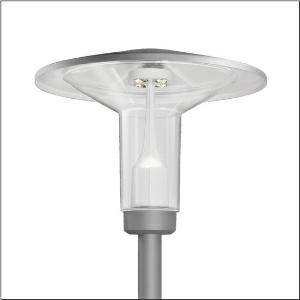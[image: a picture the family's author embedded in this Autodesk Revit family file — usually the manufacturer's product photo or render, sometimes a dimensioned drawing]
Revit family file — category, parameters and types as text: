
# Revit family: laterne_iq___st1_2a_5xa5255mf14h_e85f
name_source: partatom
category: Lighting Fixtures
units: mm (PartAtom-declared; Revit-internal decimal feet)

## family parameters
Cut with Voids When Loaded = No
Host = Face
Light Source = No
Part Type = Normal
Room Calculation Point = No
Round Connector Dimension = Use Diameter
Shared = No

## types (1)
- --- (1 x LED, 1540 lm, 11.8 W, 2700K)
    Apparent Load = 12 VA
    CIE Flux Codes = 25 63 94 98 100
    Color Rendering = 70
    Color Temperature = 2700K
    Default Elevation = 1800 mm
    Description = Lantern iQ, mast luminaire, Module 540 iQ-SR, primary light control with 3 zone facetted reflector, of plastic, silver coated, highly specular, structured, primary optical cover: cover, of PMMA, transparent, light distribution: ST1.2a, light emission: direct distribution, primary light characteristic: asymmetric, installation type: post-top, LED, High Power LED, rated luminous flux: 1.540lm, luminous efficacy: 131lm/W, light colour: 727, colour temperature: 2700K, control gear: ECG iQ, control: presetting dimming logarithmic, Street-Remote, Auto-Match, Temp-Guard, Lumen-Switch, Night-Set, Smart-Wire, Light-Fading, Desk-Remote (wireless, voltage-free reading and setting of iQ features in the workshop via application-optimized NFC function/RFID function), optimised constant luminous flux control (CLO 2.0), with terminal, 6-pole, max. 2.5mm², mains connection: 230..240V, AC, 50/60Hz, start of lifetime: 12W, end of service life: 12W, reduction: 6W, luminaire housing, upper part, of glass-fibre reinforced polyester, coated, Siteco® metallic grey (DB 702S), diameter: 750mm, height: 583mm, spigot size: d x l = 76 x 70mm (post-top) | with reducer (optional accessory) 60 x 70mm, post-top mast mounting element, of diecast aluminium, coated, Siteco® metallic grey (DB 702S), Module 540 iQ-SR, traffic white (RAL 9016), equipment: standard, protection rating (complete): IP65, insulation class (complete): insulation class II (safety insulation), certification: CE, ENEC, VDE, packaging unit: 1 piece

Light Distribution: ST1.2a
    Height = 583 mm
    Lamp = 1 x LED
    Lamp Light Flux = 1540 lm
    Lamp Power = 11.8 W
    Lamp count = 1
    Length = 750 mm
    Luminous efficacy = 131 lm/W
    Manufacturer = Siteco
    ModVariant = No
    Model = 5XA5255MF14H
    Number of Poles = 1
    OnlyDefault = Yes
    Power Factor = 1
    Product Name = Laterne iQ | ST1.2a
    Product group = mast luminaire | pylon top
    ProductGroupID = 6100
    Protection Class = Protection class II
    Protection Degree = IP 65
    RLX_Detail_Level = 1
    RLX_Emergency_Light_Flux = 0 lm
    RLX_Emergency_Type = 0
    RLX_Emergency_Type_DB = No
    RlxData = <blob elided: 103049 chars, md5=293a5602>
    Socket = socket
    Standby Power = 0 W
    System Light Flux = 1540 lm
    System Power = 12 W
    Type Comments = factory setting: luminous flux: 100 % | dim-lin: 254 | 472 mA
    Type Image = l_1006050.jpg
    URL = http://relux.com
    VarID = @adj_085711
    Voltage = 0 V
    Weight = 0.00 kg
    Width = 0 mm  [stored 0 ft]

note: [stored X ft] marks values corroborated as IEEE doubles in the binary element streams (Revit-internal decimal feet)

## geometry (parser evidence)
native form markers: Blend x4, Sweep x10
no freeform markers — native parametric forms only
